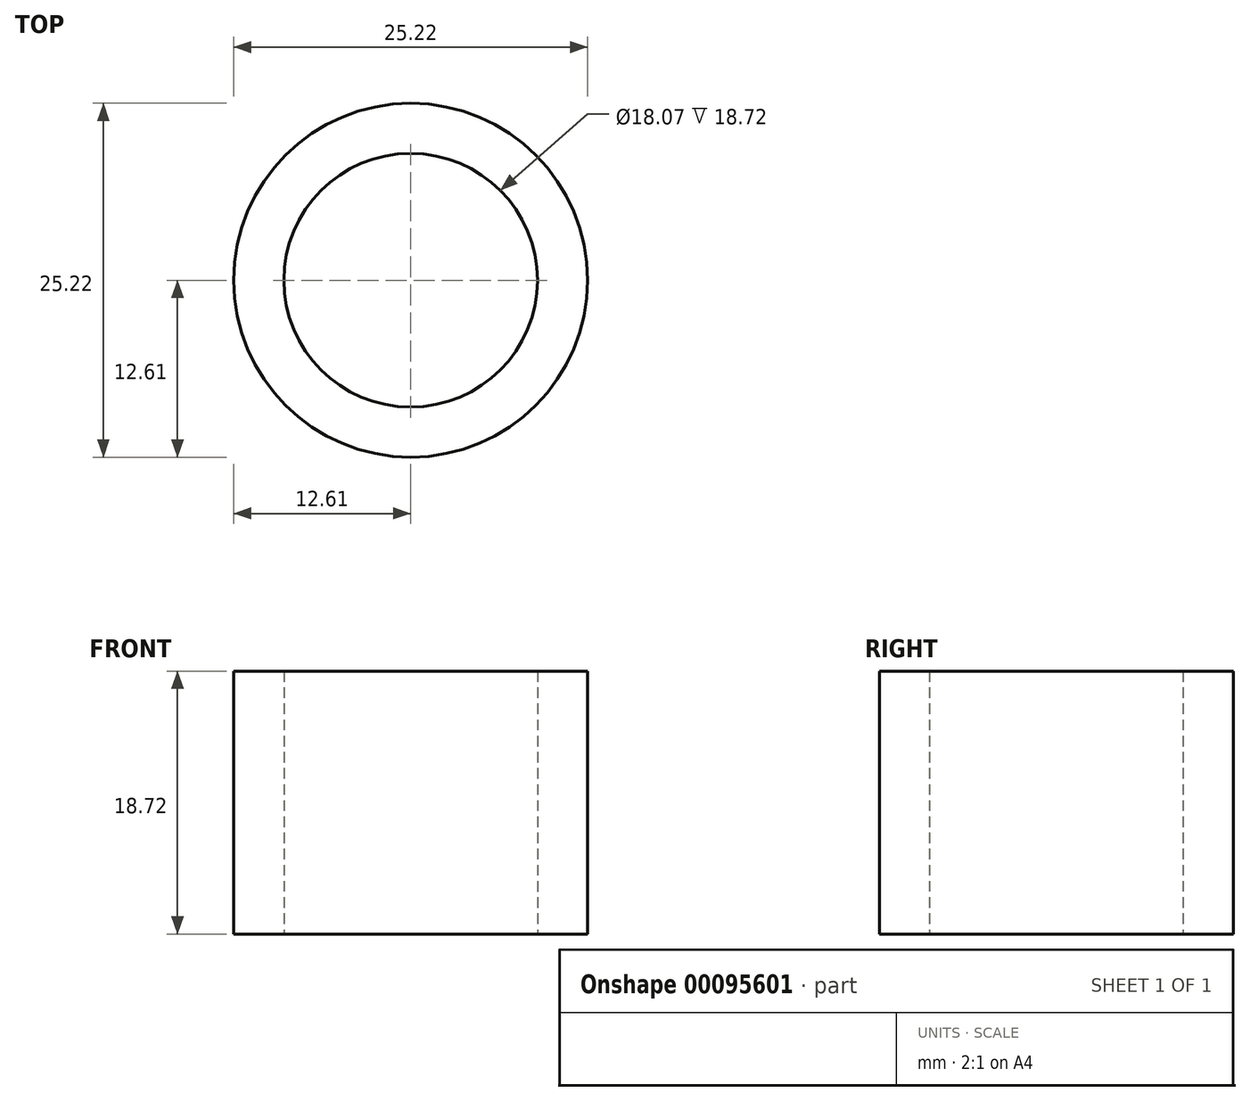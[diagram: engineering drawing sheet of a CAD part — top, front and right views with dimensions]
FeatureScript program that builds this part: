
annotation { "Feature Type Name" : "Feature", "Feature Type Description" : "" }
export const myFeature = defineFeature(function(context is Context, id is Id, definition is map)
    precondition{}
    {
        {
            var Q0;
            Q0=qCreatedBy(makeId("Top.planeOp"),FACE);
            var sketch = newSketch(context, id + "F0", { "sketchPlane" : qUnion([Q0])});
            skCircle(sketch, "E0", {"center": v(0, 0) * mm, "radius": 9.04 * mm});
            skCircle(sketch, "E1", {"center": v(0, 0) * mm, "radius": 12.6 * mm});
            skSolve(sketch);
        }
        {
            var Q0;
            Q0=makeQuery(id+"F0.imprint","IMPRINT",FACE,{"disambiguationData":[TD([[makeQuery(id+"F0.imprint","IMPRINT",EDGE,{"derivedFrom":sQuery(id+"F0.wireOp",EDGE,"E0")}),-1.0]])]});
            extrude(context, id + "F1", {"entities" : qUnion([Q0]), "depth" : 18.72 * mm});
        }
    });
